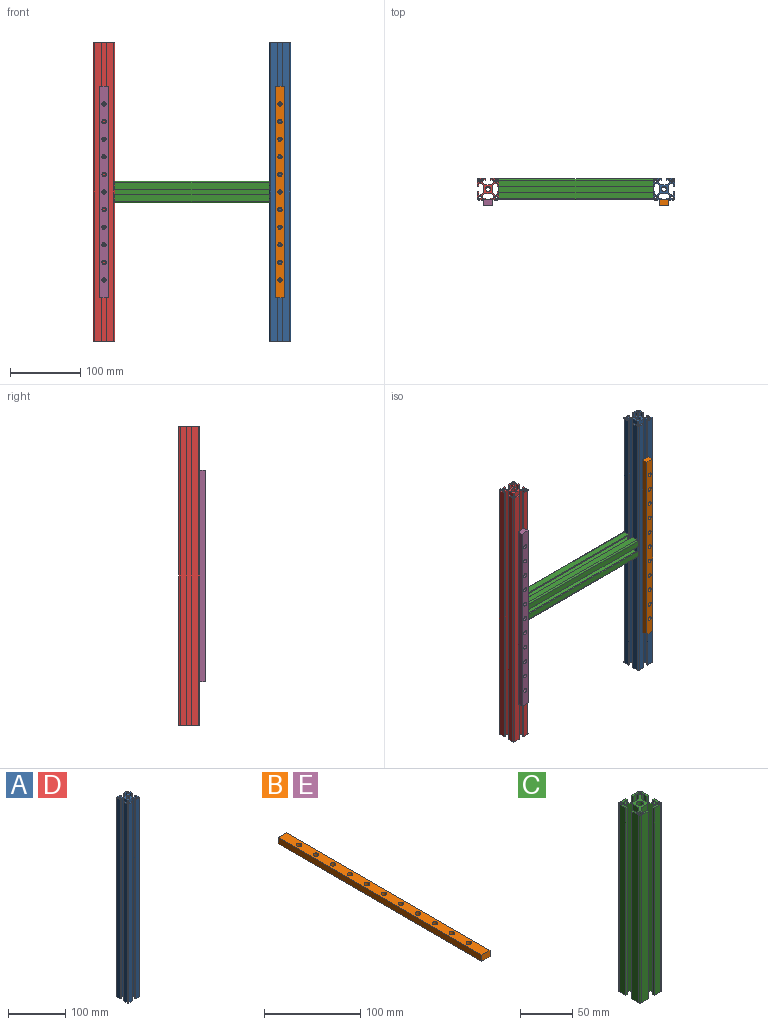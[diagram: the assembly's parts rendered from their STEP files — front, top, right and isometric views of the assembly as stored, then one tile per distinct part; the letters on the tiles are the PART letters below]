
ASSEMBLY  parts=5 mates=4
PART A: 55 faces, bbox 30x30x424 mm
  f0: plane 424x3.66mm, normal (-0.71,-0.71,0), area 2197.2mm2, adj f1,f47,f49,f50
  f1: plane 424x9.17mm, normal (-1,0,0), area 3888.7mm2, adj f0,f2,f49,f50
  f2: plane 424x3.66mm, normal (-0.71,0.71,0), area 2197.2mm2, adj f1,f3,f49,f50
  f3: plane 424x3.34mm, normal (0,1,0), area 1414.4mm2, adj f2,f4,f49,f50
  f4: plane 424x4.25mm, normal (1,0,0), area 1802mm2, adj f3,f5,f49,f50
  f5: plane 424x2mm, normal (0,1,0), area 848mm2, adj f4,f6,f49,f50
  f6: plane 424x9mm, normal (-1,0,0), area 3816mm2, adj f5,f49,f50,f54
  f7: plane 424x9mm, normal (0,-1,0), area 3816mm2, adj f8,f49,f50,f54
  f8: plane 424x2mm, normal (1,0,0), area 848mm2, adj f7,f9,f49,f50
  f9: plane 424x4.25mm, normal (0,1,0), area 1802mm2, adj f8,f10,f49,f50
  f10: plane 424x3.34mm, normal (1,0,0), area 1414.4mm2, adj f9,f11,f49,f50
  f11: plane 424x3.66mm, normal (0.71,-0.71,0), area 2197.2mm2, adj f10,f12,f49,f50
  f12: plane 424x9.17mm, normal (0,-1,0), area 3888.7mm2, adj f11,f13,f49,f50
  f13: plane 424x3.66mm, normal (-0.71,-0.71,0), area 2197.2mm2, adj f12,f14,f49,f50
  f14: plane 424x3.34mm, normal (-1,0,0), area 1414.4mm2, adj f13,f15,f49,f50
  f15: plane 424x4.25mm, normal (0,1,0), area 1802mm2, adj f14,f16,f49,f50
  f16: plane 424x2mm, normal (-1,0,0), area 848mm2, adj f15,f17,f49,f50
  f17: plane 424x9mm, normal (0,-1,0), area 3816mm2, adj f16,f49,f50,f53
  f18: plane 424x9mm, normal (1,0,0), area 3816mm2, adj f19,f49,f50,f53
  f19: plane 424x2mm, normal (0,1,0), area 848mm2, adj f18,f20,f49,f50
  f20: plane 424x4.25mm, normal (-1,0,0), area 1802mm2, adj f19,f21,f49,f50
  f21: plane 424x3.34mm, normal (0,1,0), area 1414.4mm2, adj f20,f22,f49,f50
  f22: plane 424x3.66mm, normal (0.71,0.71,0), area 2197.2mm2, adj f21,f23,f49,f50
  f23: plane 424x9.17mm, normal (1,0,0), area 3888.7mm2, adj f22,f24,f49,f50
  f24: plane 424x3.66mm, normal (0.71,-0.71,0), area 2197.2mm2, adj f23,f25,f49,f50
  f25: plane 424x3.34mm, normal (0,-1,0), area 1414.4mm2, adj f24,f26,f49,f50
  f26: plane 424x4.25mm, normal (-1,0,0), area 1802mm2, adj f25,f27,f49,f50
  f27: plane 424x2mm, normal (0,-1,0), area 848mm2, adj f26,f28,f49,f50
  f28: plane 424x9mm, normal (1,0,0), area 3816mm2, adj f27,f49,f50,f52
  f29: plane 424x9mm, normal (0,1,0), area 3816mm2, adj f30,f49,f50,f52
  f30: plane 424x2mm, normal (-1,0,0), area 848mm2, adj f29,f31,f49,f50
  f31: plane 424x4.25mm, normal (0,-1,0), area 1802mm2, adj f30,f32,f49,f50
  f32: plane 424x3.34mm, normal (-1,0,0), area 1414.4mm2, adj f31,f33,f49,f50
  f33: plane 424x3.66mm, normal (-0.71,0.71,0), area 2197.2mm2, adj f32,f34,f49,f50
  f34: plane 424x9.17mm, normal (0,1,0), area 3888.7mm2, adj f33,f35,f49,f50
  f35: plane 424x3.66mm, normal (0.71,0.71,0), area 2197.2mm2, adj f34,f36,f49,f50
  f36: plane 424x3.34mm, normal (1,0,0), area 1414.4mm2, adj f35,f37,f49,f50
  f37: plane 424x4.25mm, normal (0,-1,0), area 1802mm2, adj f36,f38,f49,f50
  f38: plane 424x2mm, normal (1,0,0), area 848mm2, adj f37,f39,f49,f50
  f39: plane 424x9mm, normal (0,1,0), area 3816mm2, adj f38,f49,f50,f51
  f40: plane 424x9mm, normal (-1,0,0), area 3816mm2, adj f41,f49,f50,f51
  f41: plane 424x2mm, normal (0,-1,0), area 848mm2, adj f40,f42,f49,f50
  f42: plane 424x4.25mm, normal (1,0,0), area 1802mm2, adj f41,f47,f49,f50
  f43: cylinder r=2mm len=424mm, axis (0,0,-1), area 5328.1mm2, adj f49,f50
  f44: cylinder r=2mm len=424mm, axis (0,0,-1), area 5328.1mm2, adj f49,f50
  f45: cylinder r=3.4mm len=424mm, axis (0,0,-1), area 9057.8mm2, adj f49,f50
  f46: cylinder r=2mm len=424mm, axis (0,0,-1), area 5328.1mm2, adj f49,f50
  f47: plane 424x3.34mm, normal (0,-1,0), area 1414.4mm2, adj f0,f42,f49,f50
  f48: cylinder r=2mm len=424mm, axis (0,0,-1), area 5328.1mm2, adj f49,f50
  f49: plane 30x30mm, normal (0,0,1), area 337.7mm2, adj f0,f1,f2,f3,f4,f5,f6,f7
  f50: plane 30x30mm, normal (0,0,-1), area 337.7mm2, adj f0,f1,f2,f3,f4,f5,f6,f7
  f51: cylinder r=2mm len=424mm, axis (0,0,-1), area 1332mm2, adj f39,f40,f49,f50
  f52: cylinder r=2mm len=424mm, axis (0,0,1), area 1332mm2, adj f28,f29,f49,f50
  f53: cylinder r=2mm len=424mm, axis (0,0,-1), area 1332mm2, adj f17,f18,f49,f50
  f54: cylinder r=2mm len=424mm, axis (0,0,1), area 1332mm2, adj f6,f7,f49,f50
PART B: 39 faces, bbox 12x300x8 mm
  f0: plane 12x8mm, normal (0,-1,0), area 96mm2, adj f1,f3,f4,f5
  f1: plane 300x8mm, normal (1,0,0), area 2400mm2, adj f0,f2,f4,f5
  f2: plane 12x8mm, normal (0,1,0), area 96mm2, adj f1,f3,f4,f5
  f3: plane 300x8mm, normal (-1,0,0), area 2400mm2, adj f0,f2,f4,f5
  f4: plane 300x12mm, normal (0,0,1), area 3289mm2, adj f0,f1,f2,f3,f18,f20,f22,f24
  f5: plane 300x12mm, normal (0,0,-1), area 3494.2mm2, adj f0,f1,f2,f3,f6,f7,f8,f9
  f6: cylinder r=1.75mm len=3.5mm, axis (0,0,-1), area 38.5mm2, adj f5,f37
  f7: cylinder r=1.75mm len=3.5mm, axis (0,0,-1), area 38.5mm2, adj f5,f35
  f8: cylinder r=1.75mm len=3.5mm, axis (0,0,-1), area 38.5mm2, adj f5,f33
  f9: cylinder r=1.75mm len=3.5mm, axis (0,0,-1), area 38.5mm2, adj f5,f31
  f10: cylinder r=1.75mm len=3.5mm, axis (0,0,-1), area 38.5mm2, adj f5,f29
  f11: cylinder r=1.75mm len=3.5mm, axis (0,0,-1), area 38.5mm2, adj f5,f27
  f12: cylinder r=1.75mm len=3.5mm, axis (0,0,-1), area 38.5mm2, adj f5,f25
  f13: cylinder r=1.75mm len=3.5mm, axis (0,0,-1), area 38.5mm2, adj f5,f23
  f14: cylinder r=1.75mm len=3.5mm, axis (0,0,-1), area 38.5mm2, adj f5,f21
  f15: cylinder r=1.75mm len=3.5mm, axis (0,0,-1), area 38.5mm2, adj f5,f19
  f16: cylinder r=1.75mm len=3.5mm, axis (0,0,-1), area 38.5mm2, adj f5,f17
  f17: plane 6x6mm, normal (0,0,1), area 18.7mm2, adj f16,f18
  f18: cylinder r=3mm len=6mm, axis (0,0,1), area 84.8mm2, adj f4,f17
  f19: plane 6x6mm, normal (0,0,1), area 18.7mm2, adj f15,f20
  f20: cylinder r=3mm len=6mm, axis (0,0,1), area 84.8mm2, adj f4,f19
  f21: plane 6x6mm, normal (0,0,1), area 18.7mm2, adj f14,f22
  f22: cylinder r=3mm len=6mm, axis (0,0,1), area 84.8mm2, adj f4,f21
  f23: plane 6x6mm, normal (0,0,1), area 18.7mm2, adj f13,f24
  f24: cylinder r=3mm len=6mm, axis (0,0,1), area 84.8mm2, adj f4,f23
  f25: plane 6x6mm, normal (0,0,1), area 18.7mm2, adj f12,f26
  f26: cylinder r=3mm len=6mm, axis (0,0,1), area 84.8mm2, adj f4,f25
  f27: plane 6x6mm, normal (0,0,1), area 18.7mm2, adj f11,f28
  f28: cylinder r=3mm len=6mm, axis (0,0,1), area 84.8mm2, adj f4,f27
  f29: plane 6x6mm, normal (0,0,1), area 18.7mm2, adj f10,f30
  f30: cylinder r=3mm len=6mm, axis (0,0,1), area 84.8mm2, adj f4,f29
  f31: plane 6x6mm, normal (0,0,1), area 18.7mm2, adj f9,f32
  f32: cylinder r=3mm len=6mm, axis (0,0,1), area 84.8mm2, adj f4,f31
  f33: plane 6x6mm, normal (0,0,1), area 18.7mm2, adj f8,f34
  f34: cylinder r=3mm len=6mm, axis (0,0,1), area 84.8mm2, adj f4,f33
  f35: plane 6x6mm, normal (0,0,1), area 18.7mm2, adj f7,f36
  f36: cylinder r=3mm len=6mm, axis (0,0,1), area 84.8mm2, adj f4,f35
  f37: plane 6x6mm, normal (0,0,1), area 18.7mm2, adj f6,f38
  f38: cylinder r=3mm len=6mm, axis (0,0,1), area 84.8mm2, adj f4,f37
PART C: 55 faces, bbox 30x30x220 mm
  f0: plane 220x3.66mm, normal (-0.71,-0.71,0), area 1140mm2, adj f1,f47,f49,f50
  f1: plane 220x9.17mm, normal (-1,0,0), area 2017.7mm2, adj f0,f2,f49,f50
  f2: plane 220x3.66mm, normal (-0.71,0.71,0), area 1140mm2, adj f1,f3,f49,f50
  f3: plane 220x3.34mm, normal (0,1,0), area 733.9mm2, adj f2,f4,f49,f50
  f4: plane 220x4.25mm, normal (1,0,0), area 935mm2, adj f3,f5,f49,f50
  f5: plane 220x2mm, normal (0,1,0), area 440mm2, adj f4,f6,f49,f50
  f6: plane 220x9mm, normal (-1,0,0), area 1980mm2, adj f5,f49,f50,f54
  f7: plane 220x9mm, normal (0,-1,0), area 1980mm2, adj f8,f49,f50,f54
  f8: plane 220x2mm, normal (1,0,0), area 440mm2, adj f7,f9,f49,f50
  f9: plane 220x4.25mm, normal (0,1,0), area 935mm2, adj f8,f10,f49,f50
  f10: plane 220x3.34mm, normal (1,0,0), area 733.9mm2, adj f9,f11,f49,f50
  f11: plane 220x3.66mm, normal (0.71,-0.71,0), area 1140mm2, adj f10,f12,f49,f50
  f12: plane 220x9.17mm, normal (0,-1,0), area 2017.7mm2, adj f11,f13,f49,f50
  f13: plane 220x3.66mm, normal (-0.71,-0.71,0), area 1140mm2, adj f12,f14,f49,f50
  f14: plane 220x3.34mm, normal (-1,0,0), area 733.9mm2, adj f13,f15,f49,f50
  f15: plane 220x4.25mm, normal (0,1,0), area 935mm2, adj f14,f16,f49,f50
  f16: plane 220x2mm, normal (-1,0,0), area 440mm2, adj f15,f17,f49,f50
  f17: plane 220x9mm, normal (0,-1,0), area 1980mm2, adj f16,f49,f50,f53
  f18: plane 220x9mm, normal (1,0,0), area 1980mm2, adj f19,f49,f50,f53
  f19: plane 220x2mm, normal (0,1,0), area 440mm2, adj f18,f20,f49,f50
  f20: plane 220x4.25mm, normal (-1,0,0), area 935mm2, adj f19,f21,f49,f50
  f21: plane 220x3.34mm, normal (0,1,0), area 733.9mm2, adj f20,f22,f49,f50
  f22: plane 220x3.66mm, normal (0.71,0.71,0), area 1140mm2, adj f21,f23,f49,f50
  f23: plane 220x9.17mm, normal (1,0,0), area 2017.7mm2, adj f22,f24,f49,f50
  f24: plane 220x3.66mm, normal (0.71,-0.71,0), area 1140mm2, adj f23,f25,f49,f50
  f25: plane 220x3.34mm, normal (0,-1,0), area 733.9mm2, adj f24,f26,f49,f50
  f26: plane 220x4.25mm, normal (-1,0,0), area 935mm2, adj f25,f27,f49,f50
  f27: plane 220x2mm, normal (0,-1,0), area 440mm2, adj f26,f28,f49,f50
  f28: plane 220x9mm, normal (1,0,0), area 1980mm2, adj f27,f49,f50,f52
  f29: plane 220x9mm, normal (0,1,0), area 1980mm2, adj f30,f49,f50,f52
  f30: plane 220x2mm, normal (-1,0,0), area 440mm2, adj f29,f31,f49,f50
  f31: plane 220x4.25mm, normal (0,-1,0), area 935mm2, adj f30,f32,f49,f50
  f32: plane 220x3.34mm, normal (-1,0,0), area 733.9mm2, adj f31,f33,f49,f50
  f33: plane 220x3.66mm, normal (-0.71,0.71,0), area 1140mm2, adj f32,f34,f49,f50
  f34: plane 220x9.17mm, normal (0,1,0), area 2017.7mm2, adj f33,f35,f49,f50
  f35: plane 220x3.66mm, normal (0.71,0.71,0), area 1140mm2, adj f34,f36,f49,f50
  f36: plane 220x3.34mm, normal (1,0,0), area 733.9mm2, adj f35,f37,f49,f50
  f37: plane 220x4.25mm, normal (0,-1,0), area 935mm2, adj f36,f38,f49,f50
  f38: plane 220x2mm, normal (1,0,0), area 440mm2, adj f37,f39,f49,f50
  f39: plane 220x9mm, normal (0,1,0), area 1980mm2, adj f38,f49,f50,f51
  f40: plane 220x9mm, normal (-1,0,0), area 1980mm2, adj f41,f49,f50,f51
  f41: plane 220x2mm, normal (0,-1,0), area 440mm2, adj f40,f42,f49,f50
  f42: plane 220x4.25mm, normal (1,0,0), area 935mm2, adj f41,f47,f49,f50
  f43: cylinder r=2mm len=220mm, axis (0,0,-1), area 2764.6mm2, adj f49,f50
  f44: cylinder r=2mm len=220mm, axis (0,0,-1), area 2764.6mm2, adj f49,f50
  f45: cylinder r=3.4mm len=220mm, axis (0,0,-1), area 4699.8mm2, adj f49,f50
  f46: cylinder r=2mm len=220mm, axis (0,0,-1), area 2764.6mm2, adj f49,f50
  f47: plane 220x3.34mm, normal (0,-1,0), area 733.9mm2, adj f0,f42,f49,f50
  f48: cylinder r=2mm len=220mm, axis (0,0,-1), area 2764.6mm2, adj f49,f50
  f49: plane 30x30mm, normal (0,0,1), area 337.7mm2, adj f0,f1,f2,f3,f4,f5,f6,f7
  f50: plane 30x30mm, normal (0,0,-1), area 337.7mm2, adj f0,f1,f2,f3,f4,f5,f6,f7
  f51: cylinder r=2mm len=220mm, axis (0,0,-1), area 691.2mm2, adj f39,f40,f49,f50
  f52: cylinder r=2mm len=220mm, axis (0,0,1), area 691.2mm2, adj f28,f29,f49,f50
  f53: cylinder r=2mm len=220mm, axis (0,0,-1), area 691.2mm2, adj f17,f18,f49,f50
  f54: cylinder r=2mm len=220mm, axis (0,0,1), area 691.2mm2, adj f6,f7,f49,f50
PART D: same geometry as A
PART E: same geometry as B
PLACE A t=(103.09,107.86,-74.53)mm
PLACE B rot(axis=(1,0,0),90deg) t=(28.09,92.86,137.47)mm
PLACE C rot(axis=(0.71,0,-0.71),180deg) t=(13.09,107.86,62.47)mm
PLACE D t=(-146.91,107.86,-74.53)mm
PLACE E rot(axis=(1,0,0),90deg) t=(-221.91,92.86,137.47)mm
MATE fastened C.f45 <-> D.f18  axis (-1,0,0) through (-206.91,107.86,137.47)mm
MATE fastened C.f45 <-> A.f6  axis (1,0,0) through (13.09,107.86,137.47)mm
MATE fastened E.f11 <-> D.f17  axis (0,1,0) through (-221.91,92.86,137.47)mm
MATE fastened B.f11 <-> A.f17  axis (0,1,0) through (28.09,92.86,137.47)mm
